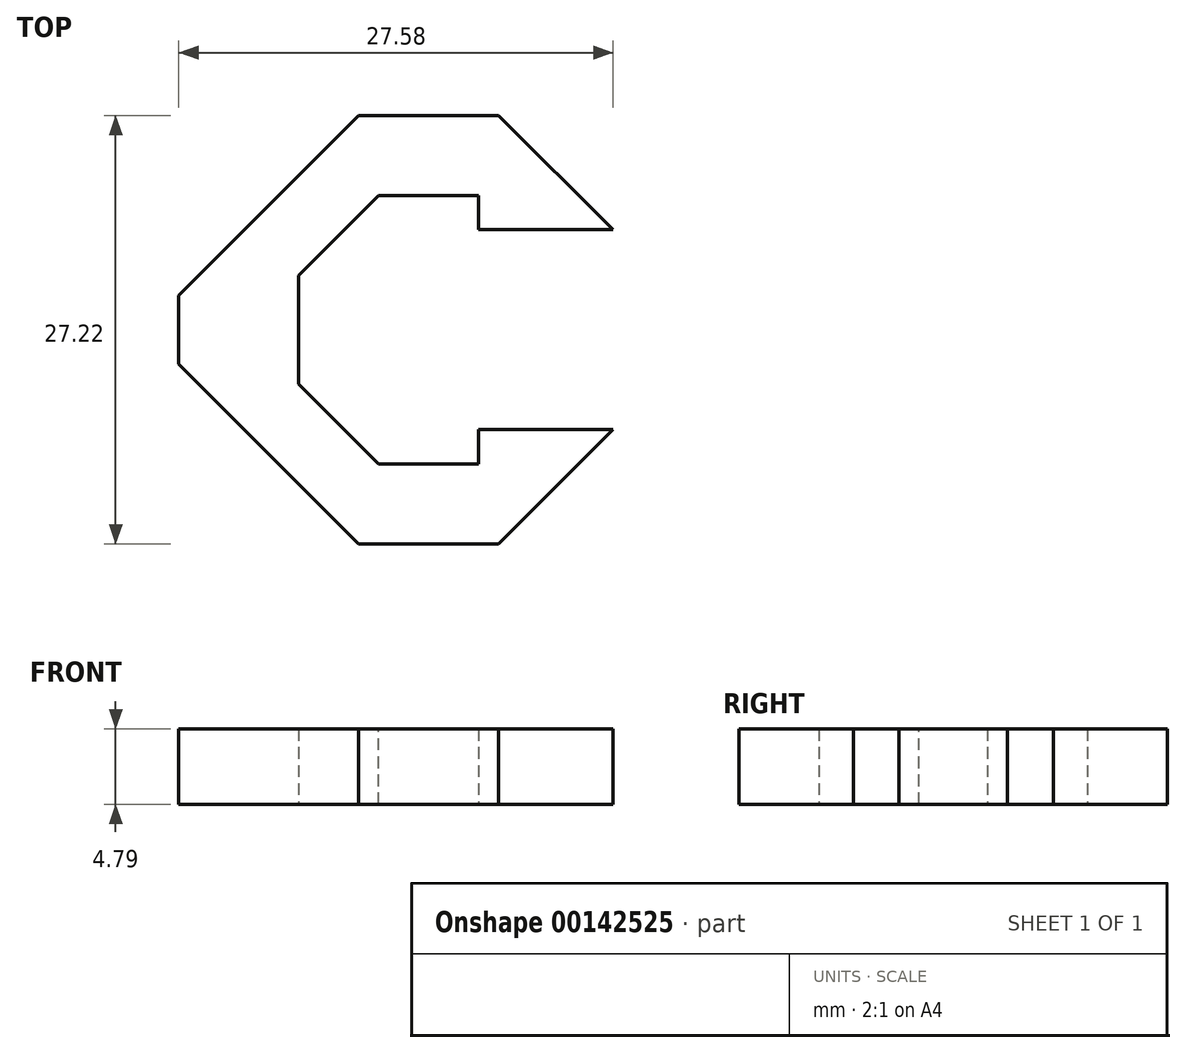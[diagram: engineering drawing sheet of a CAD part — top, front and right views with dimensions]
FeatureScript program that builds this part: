
annotation { "Feature Type Name" : "Feature", "Feature Type Description" : "" }
export const myFeature = defineFeature(function(context is Context, id is Id, definition is map)
    precondition{}
    {
        {
            var Q0;
            Q0=qCreatedBy(makeId("Top.planeOp"),FACE);
            var sketch = newSketch(context, id + "F0", { "sketchPlane" : qUnion([Q0])});
            skLineSegment(sketch, "E0", {"start": v(-37.31, 11.82) * mm, "end": v(-50.01, 11.82) * mm});
            skLineSegment(sketch, "E1", {"start": v(-50.01, 11.82) * mm, "end": v(-50.01, 14) * mm});
            skLineSegment(sketch, "E2", {"start": v(-50.01, 14) * mm, "end": v(-61.44, 14) * mm});
            skLineSegment(sketch, "E3", {"start": v(-61.44, 14) * mm, "end": v(-61.44, -3.06) * mm});
            skLineSegment(sketch, "E4", {"start": v(-61.44, -3.06) * mm, "end": v(-50.01, -3.06) * mm});
            skLineSegment(sketch, "E5", {"start": v(-50.01, -3.06) * mm, "end": v(-50.01, -0.88) * mm});
            skLineSegment(sketch, "E6", {"start": v(-50.01, -0.88) * mm, "end": v(-37.31, -0.88) * mm});
            skLineSegment(sketch, "E7", {"start": v(-37.31, 11.82) * mm, "end": v(-37.31, 19.08) * mm});
            skLineSegment(sketch, "E8", {"start": v(-37.31, 19.08) * mm, "end": v(-69.06, 19.08) * mm});
            skLineSegment(sketch, "E9", {"start": v(-69.06, 19.08) * mm, "end": v(-69.06, -8.14) * mm});
            skLineSegment(sketch, "E10", {"start": v(-69.06, -8.14) * mm, "end": v(-37.31, -8.14) * mm});
            skLineSegment(sketch, "E11", {"start": v(-37.31, -8.14) * mm, "end": v(-37.31, -0.88) * mm});
            skSolve(sketch);
        }
        {
            var Q0;
            Q0=makeQuery(id+"F0.imprint","IMPRINT",FACE,{"disambiguationData":[TD([[makeQuery(id+"F0.imprint","IMPRINT",EDGE,{"derivedFrom":sQuery(id+"F0.wireOp",EDGE,"E0")}),-1.0]])]});
            extrude(context, id + "F1", {"entities" : qUnion([Q0]), "depth" : 4.8 * mm});
        }
        {
            var Q0;
            Q0=makeQuery(id+"F1.opExtrude","SWEPT_EDGE",EDGE,{"disambiguationData":[OSD([sQuery(id+"F0.wireOp",EDGE,"E8"),sQuery(id+"F0.wireOp",EDGE,"E9")])]});
            var Q1;
            Q1=makeQuery(id+"F1.opExtrude","SWEPT_EDGE",EDGE,{"disambiguationData":[OSD([sQuery(id+"F0.wireOp",EDGE,"E7"),sQuery(id+"F0.wireOp",EDGE,"E8")])]});
            var Q2;
            Q2=makeQuery(id+"F1.opExtrude","SWEPT_EDGE",EDGE,{"disambiguationData":[OSD([sQuery(id+"F0.wireOp",EDGE,"E10"),sQuery(id+"F0.wireOp",EDGE,"E11")])]});
            var Q3;
            Q3=makeQuery(id+"F1.opExtrude","SWEPT_EDGE",EDGE,{"disambiguationData":[OSD([sQuery(id+"F0.wireOp",EDGE,"E9"),sQuery(id+"F0.wireOp",EDGE,"E10")])]});
            chamfer(context, id + "F2", {"entities" : qUnion([Q0, Q1, Q2, Q3]), "width" : 11.43 * mm, "tangentPropagation" : true});
        }
        {
            var Q0;
            Q0=makeQuery(id+"F1.opExtrude","SWEPT_EDGE",EDGE,{"disambiguationData":[OSD([sQuery(id+"F0.wireOp",EDGE,"E2"),sQuery(id+"F0.wireOp",EDGE,"E3")])]});
            var Q1;
            Q1=makeQuery(id+"F1.opExtrude","SWEPT_EDGE",EDGE,{"disambiguationData":[OSD([sQuery(id+"F0.wireOp",EDGE,"E3"),sQuery(id+"F0.wireOp",EDGE,"E4")])]});
            chamfer(context, id + "F3", {"entities" : qUnion([Q0, Q1]), "width" : 5.08 * mm, "tangentPropagation" : true});
        }
    });
